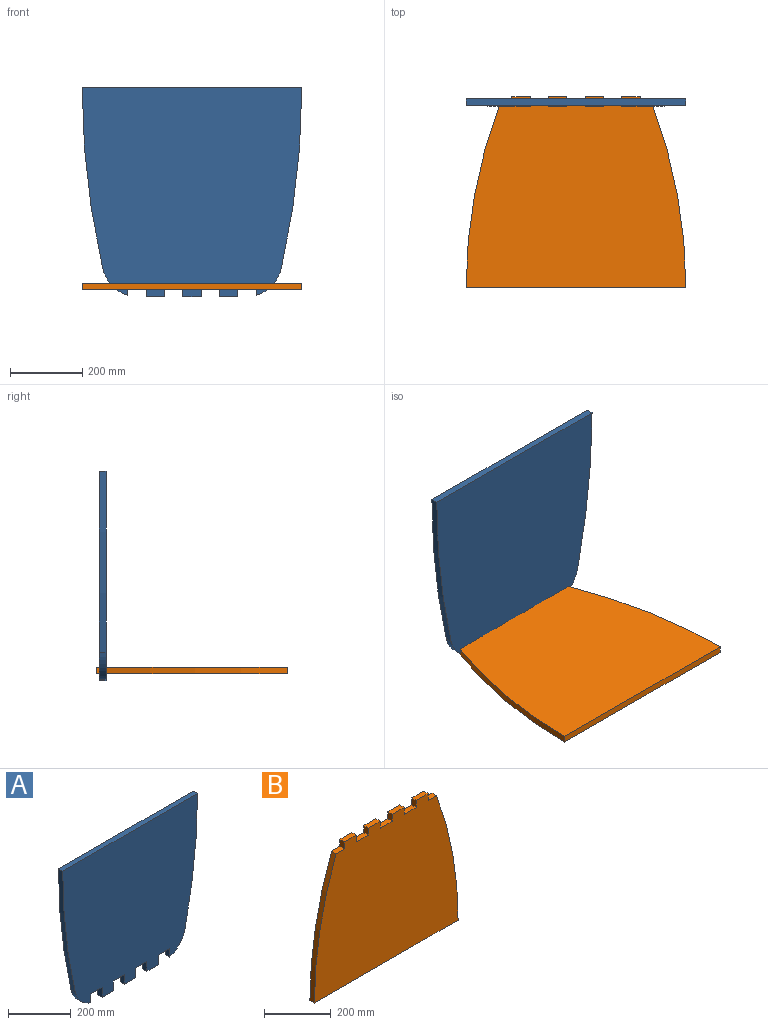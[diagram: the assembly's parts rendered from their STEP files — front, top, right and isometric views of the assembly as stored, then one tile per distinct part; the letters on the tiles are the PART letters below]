
ASSEMBLY  parts=2 mates=1
PART A: 22 faces, bbox 609.6x19.1x581.9 mm
  f0: plane 50.8x19.05mm, normal (0,0,-1), area 967.7mm2, adj f1,f19,f20,f21
  f1: plane 33.84x19.05mm, normal (-1,0,0), area 644.6mm2, adj f0,f2,f20,f21
  f2: cylinder r=101.6mm len=74.56mm, axis (0,1,0), area 2040mm2, adj f1,f3,f20,f21
  f3: cylinder r=2244.5mm len=503.09mm, axis (0,1,0), area 9665.9mm2, adj f2,f4,f20,f21
  f4: plane 609.6x19.05mm, normal (0,0,1), area 11612.9mm2, adj f3,f5,f20,f21
  f5: cylinder r=2244.5mm len=503.09mm, axis (0,1,0), area 9665.9mm2, adj f4,f6,f20,f21
  f6: cylinder r=101.6mm len=74.56mm, axis (0,1,0), area 2040mm2, adj f5,f7,f20,f21
  f7: plane 33.84x19.05mm, normal (1,0,0), area 644.6mm2, adj f6,f8,f20,f21
  f8: plane 50.8x19.05mm, normal (0,0,-1), area 967.7mm2, adj f7,f9,f20,f21
  f9: plane 38.1x19.05mm, normal (-1,0,0), area 725.8mm2, adj f8,f10,f20,f21
  f10: plane 50.8x19.05mm, normal (0,0,-1), area 967.7mm2, adj f9,f11,f20,f21
  f11: plane 38.1x19.05mm, normal (1,0,0), area 725.8mm2, adj f10,f12,f20,f21
  f12: plane 50.8x19.05mm, normal (0,0,-1), area 967.7mm2, adj f11,f13,f20,f21
  f13: plane 38.1x19.05mm, normal (-1,0,0), area 725.8mm2, adj f12,f14,f20,f21
  f14: plane 50.8x19.05mm, normal (0,0,-1), area 967.7mm2, adj f13,f15,f20,f21
  f15: plane 38.1x19.05mm, normal (1,0,0), area 725.8mm2, adj f14,f16,f20,f21
  f16: plane 50.8x19.05mm, normal (0,0,-1), area 967.7mm2, adj f15,f17,f20,f21
  f17: plane 38.1x19.05mm, normal (-1,0,0), area 725.8mm2, adj f16,f18,f20,f21
  f18: plane 50.8x19.05mm, normal (0,0,-1), area 967.7mm2, adj f17,f19,f20,f21
  f19: plane 38.1x19.05mm, normal (1,0,0), area 725.8mm2, adj f0,f18,f20,f21
  f20: plane 609.6x581.91mm, normal (0,-1,0), area 315032.8mm2, adj f0,f1,f2,f3,f4,f5,f6,f7
  f21: plane 609.6x581.91mm, normal (0,1,0), area 315032.8mm2, adj f0,f1,f2,f3,f4,f5,f6,f7
PART B: 22 faces, bbox 609.6x19.1x528 mm
  f0: plane 35.27x19.05mm, normal (0,0,1), area 671.9mm2, adj f1,f19,f20,f21
  f1: cylinder r=1422.85mm len=502.62mm, axis (0,1,0), area 9786mm2, adj f0,f2,f20,f21
  f2: plane 609.6x19.05mm, normal (0,0,-1), area 11612.9mm2, adj f1,f3,f20,f21
  f3: cylinder r=1422.85mm len=502.62mm, axis (0,1,0), area 9786mm2, adj f2,f4,f20,f21
  f4: plane 35.27x19.05mm, normal (0,0,1), area 671.9mm2, adj f3,f5,f20,f21
  f5: plane 25.4x19.05mm, normal (1,0,0), area 483.9mm2, adj f4,f6,f20,f21
  f6: plane 50.8x19.05mm, normal (0,0,1), area 967.7mm2, adj f5,f7,f20,f21
  f7: plane 25.4x19.05mm, normal (-1,0,0), area 483.9mm2, adj f6,f8,f20,f21
  f8: plane 50.8x19.05mm, normal (0,0,1), area 967.7mm2, adj f7,f9,f20,f21
  f9: plane 25.4x19.05mm, normal (1,0,0), area 483.9mm2, adj f8,f10,f20,f21
  f10: plane 50.8x19.05mm, normal (0,0,1), area 967.7mm2, adj f9,f11,f20,f21
  f11: plane 25.4x19.05mm, normal (-1,0,0), area 483.9mm2, adj f10,f12,f20,f21
  f12: plane 50.8x19.05mm, normal (0,0,1), area 967.7mm2, adj f11,f13,f20,f21
  f13: plane 25.4x19.05mm, normal (1,0,0), area 483.9mm2, adj f12,f14,f20,f21
  f14: plane 50.8x19.05mm, normal (0,0,1), area 967.7mm2, adj f13,f15,f20,f21
  f15: plane 25.4x19.05mm, normal (-1,0,0), area 483.9mm2, adj f14,f16,f20,f21
  f16: plane 50.8x19.05mm, normal (0,0,1), area 967.7mm2, adj f15,f17,f20,f21
  f17: plane 25.4x19.05mm, normal (1,0,0), area 483.9mm2, adj f16,f18,f20,f21
  f18: plane 50.8x19.05mm, normal (0,0,1), area 967.7mm2, adj f17,f19,f20,f21
  f19: plane 25.4x19.05mm, normal (-1,0,0), area 483.9mm2, adj f0,f18,f20,f21
  f20: plane 609.6x528.02mm, normal (0,-1,0), area 281226.4mm2, adj f0,f1,f2,f3,f4,f5,f6,f7
  f21: plane 609.6x528.02mm, normal (0,1,0), area 281226.4mm2, adj f0,f1,f2,f3,f4,f5,f6,f7
PLACE A t=(-0.04,744.87,576)mm
PLACE B rot(axis=(-1,0,0),90deg) t=(-0.04,204.16,-88.46)mm
MATE fastened B.f16 <-> A.f20  axis (0,1,0) through (177.76,706.77,-69.41)mm
